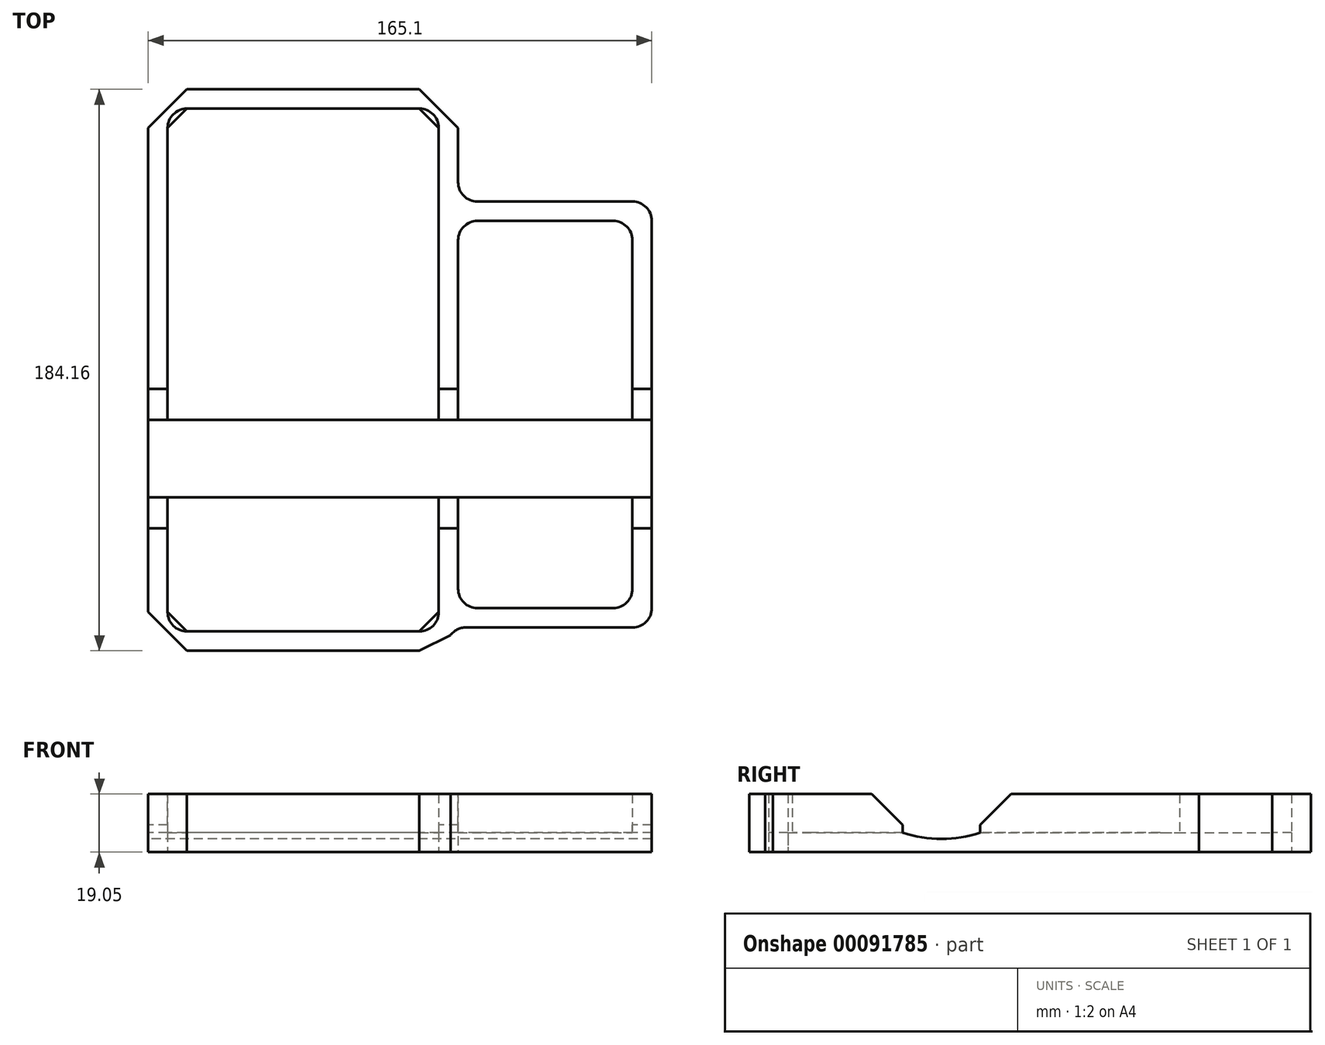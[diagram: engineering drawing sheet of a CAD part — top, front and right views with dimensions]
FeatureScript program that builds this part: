
annotation { "Feature Type Name" : "Feature", "Feature Type Description" : "" }
export const myFeature = defineFeature(function(context is Context, id is Id, definition is map)
    precondition{}
    {
        {
            var Q0;
            Q0=qCreatedBy(makeId("Top.planeOp"),FACE);
            var sketch = newSketch(context, id + "F0", { "sketchPlane" : qUnion([Q0])});
            skLineSegment(sketch, "E0.bottom", {"start": v(-38.1, 85.72) * mm, "end": v(38.1, 85.72) * mm});
            skLineSegment(sketch, "E0.top", {"start": v(-38.1, -85.73) * mm, "end": v(38.1, -85.73) * mm});
            skLineSegment(sketch, "E0.left", {"start": v(-44.45, 79.38) * mm, "end": v(-44.45, -79.38) * mm});
            skLineSegment(sketch, "E0.right", {"start": v(44.45, 79.38) * mm, "end": v(44.45, -79.38) * mm});
            skPoint(sketch, "E0.middle", {"position": v(0, 0) * mm});
            skPoint(sketch, "E1.visualSharp", {"position": v(-44.45, 85.72) * mm});
            skArc(sketch, "E1.filletArc", {"start": v(-38.1, 85.72) * mm, "mid": v(-42.6, 83.87) * mm, "end": v(-44.45, 79.38) * mm});
            skPoint(sketch, "E2.visualSharp", {"position": v(44.45, 85.72) * mm});
            skArc(sketch, "E2.filletArc", {"start": v(44.45, 79.38) * mm, "mid": v(42.6, 83.87) * mm, "end": v(38.1, 85.72) * mm});
            skPoint(sketch, "E3.visualSharp", {"position": v(44.45, -85.73) * mm});
            skArc(sketch, "E3.filletArc", {"start": v(38.1, -85.73) * mm, "mid": v(42.6, -83.87) * mm, "end": v(44.45, -79.38) * mm});
            skPoint(sketch, "E4.visualSharp", {"position": v(-44.45, -85.73) * mm});
            skArc(sketch, "E4.filletArc", {"start": v(-44.45, -79.38) * mm, "mid": v(-42.6, -83.87) * mm, "end": v(-38.1, -85.73) * mm});
            skArc(sketch, "E5.0", {"start": v(50.8, 79.38) * mm, "mid": v(47.08, 88.36) * mm, "end": v(38.1, 92.07) * mm});
            skLineSegment(sketch, "E5.1", {"start": v(-38.1, 92.08) * mm, "end": v(38.1, 92.08) * mm});
            skLineSegment(sketch, "E5.2", {"start": v(50.8, 79.38) * mm, "end": v(50.8, 61.61) * mm});
            skArc(sketch, "E5.3", {"start": v(-38.1, 92.07) * mm, "mid": v(-47.08, 88.36) * mm, "end": v(-50.8, 79.38) * mm});
            skArc(sketch, "E5.4", {"start": v(38.1, -92.08) * mm, "mid": v(43.79, -90.73) * mm, "end": v(48.27, -86.98) * mm});
            skLineSegment(sketch, "E5.5", {"start": v(-38.1, -92.08) * mm, "end": v(38.1, -92.08) * mm});
            skArc(sketch, "E5.6", {"start": v(-50.8, -79.38) * mm, "mid": v(-47.08, -88.36) * mm, "end": v(-38.1, -92.08) * mm});
            skLineSegment(sketch, "E5.7", {"start": v(-50.8, 79.38) * mm, "end": v(-50.8, -79.38) * mm});
            skLineSegment(sketch, "E6.bottom", {"start": v(57.15, -78.09) * mm, "end": v(101.6, -78.09) * mm});
            skLineSegment(sketch, "E6.top", {"start": v(57.15, 48.91) * mm, "end": v(101.6, 48.91) * mm});
            skLineSegment(sketch, "E6.left", {"start": v(50.8, -71.74) * mm, "end": v(50.8, 42.56) * mm});
            skLineSegment(sketch, "E6.right", {"start": v(107.95, -71.74) * mm, "end": v(107.95, 42.56) * mm});
            skPoint(sketch, "E6.middle", {"position": v(79.38, -14.59) * mm});
            skLineSegment(sketch, "E7.0", {"start": v(53.35, -84.44) * mm, "end": v(107.95, -84.44) * mm});
            skLineSegment(sketch, "E7.1", {"start": v(114.3, -78.09) * mm, "end": v(114.3, 48.91) * mm});
            skLineSegment(sketch, "E7.2", {"start": v(57.15, 55.26) * mm, "end": v(107.95, 55.26) * mm});
            skPoint(sketch, "E8.visualSharp", {"position": v(107.95, 48.91) * mm});
            skArc(sketch, "E8.filletArc", {"start": v(107.95, 42.56) * mm, "mid": v(106.1, 47.05) * mm, "end": v(101.6, 48.91) * mm});
            skPoint(sketch, "E9.visualSharp", {"position": v(107.95, -78.09) * mm});
            skArc(sketch, "E9.filletArc", {"start": v(101.6, -78.09) * mm, "mid": v(106.1, -76.23) * mm, "end": v(107.95, -71.74) * mm});
            skPoint(sketch, "E10.visualSharp", {"position": v(114.3, -84.44) * mm});
            skArc(sketch, "E10.filletArc", {"start": v(107.95, -84.44) * mm, "mid": v(112.44, -82.58) * mm, "end": v(114.3, -78.09) * mm});
            skPoint(sketch, "E11.visualSharp", {"position": v(114.3, 55.26) * mm});
            skArc(sketch, "E11.filletArc", {"start": v(114.3, 48.91) * mm, "mid": v(112.44, 53.4) * mm, "end": v(107.95, 55.26) * mm});
            skArc(sketch, "E12.filletArc", {"start": v(50.8, 61.61) * mm, "mid": v(52.66, 57.12) * mm, "end": v(57.15, 55.26) * mm});
            skPoint(sketch, "E13.visualSharp", {"position": v(50.8, 48.91) * mm});
            skArc(sketch, "E13.filletArc", {"start": v(57.15, 48.91) * mm, "mid": v(52.66, 47.05) * mm, "end": v(50.8, 42.56) * mm});
            skPoint(sketch, "E14.visualSharp", {"position": v(50.8, -78.09) * mm});
            skArc(sketch, "E14.filletArc", {"start": v(50.8, -71.74) * mm, "mid": v(52.66, -76.23) * mm, "end": v(57.15, -78.09) * mm});
            skArc(sketch, "E15.filletArc", {"start": v(53.35, -84.44) * mm, "mid": v(50.5, -85.11) * mm, "end": v(48.27, -86.98) * mm});
            skLineSegment(sketch, "E16", {"start": v(38.1, 85.72) * mm, "end": v(44.45, 79.38) * mm});
            skLineSegment(sketch, "E17", {"start": v(38.1, 92.07) * mm, "end": v(50.8, 79.38) * mm});
            skLineSegment(sketch, "E18", {"start": v(-44.45, 79.38) * mm, "end": v(-38.1, 85.72) * mm});
            skLineSegment(sketch, "E19", {"start": v(-38.15, 93.54) * mm, "end": v(-47.04, 96.44) * mm});
            skLineSegment(sketch, "E20", {"start": v(-38.1, 92.08) * mm, "end": v(-50.8, 79.38) * mm});
            skLineSegment(sketch, "E21", {"start": v(-44.45, -79.38) * mm, "end": v(-38.1, -85.73) * mm});
            skLineSegment(sketch, "E22", {"start": v(-50.8, -79.38) * mm, "end": v(-38.1, -92.08) * mm});
            skLineSegment(sketch, "E23", {"start": v(38.1, -85.73) * mm, "end": v(44.45, -79.38) * mm});
            skLineSegment(sketch, "E24", {"start": v(38.1, -92.08) * mm, "end": v(48.27, -86.98) * mm});
            skSolve(sketch);
        }
        {
            var Q0;
            Q0=makeQuery(id+"F0.imprint","IMPRINT",FACE,{"disambiguationData":[TD([[makeQuery(id+"F0.imprint","IMPRINT",EDGE,{"derivedFrom":sQuery(id+"F0.wireOp",EDGE,"E0.bottom")}),-1.0]])]});
            var Q1;
            Q1=makeQuery(id+"F0.imprint","IMPRINT",FACE,{"disambiguationData":[TD([[makeQuery(id+"F0.imprint","IMPRINT",EDGE,{"derivedFrom":sQuery(id+"F0.wireOp",EDGE,"E6.bottom")}),1.0]])]});
            var Q2;
            Q2=makeQuery(id+"F0.imprint","IMPRINT",FACE,{"disambiguationData":[TD([[makeQuery(id+"F0.imprint","IMPRINT",EDGE,{"derivedFrom":sQuery(id+"F0.wireOp",EDGE,"E0.bottom")}),1.0]])]});
            extrude(context, id + "F1", {"entities" : qUnion([Q0, Q1, Q2]), "depth" : 6.35 * mm});
        }
        {
            var Q0;
            Q0=makeQuery(id+"F0.imprint","IMPRINT",FACE,{"disambiguationData":[TD([[makeQuery(id+"F0.imprint","IMPRINT",EDGE,{"derivedFrom":sQuery(id+"F0.wireOp",EDGE,"E0.bottom")}),1.0]])]});
            extrude(context, id + "F2", {"entities" : qUnion([Q0]), "operationType" : NewBodyOperationType.ADD, "depth" : 19.05 * mm});
        }
        {
            var Q0;
            Q0=qCreatedBy(makeId("Right.planeOp"),FACE);
            var sketch = newSketch(context, id + "F3", { "sketchPlane" : qUnion([Q0])});
            skLineSegment(sketch, "E25", {"start": v(-16.4, 6.35) * mm, "end": v(-16.4, 53.7) * mm});
            skLineSegment(sketch, "E26", {"start": v(-16.4, 53.7) * mm, "end": v(-41.8, 53.7) * mm});
            skLineSegment(sketch, "E27", {"start": v(-41.8, 53.7) * mm, "end": v(-41.8, 6.35) * mm});
            skArc(sketch, "E28", {"start": v(-41.8, 6.35) * mm, "mid": v(-29.1, 4.35) * mm, "end": v(-16.4, 6.35) * mm});
            skSolve(sketch);
        }
        {
            var Q0;
            Q0=makeQuery(id+"F3.imprint","IMPRINT",FACE,{"disambiguationData":[TD([[makeQuery(id+"F3.imprint","IMPRINT",EDGE,{"derivedFrom":sQuery(id+"F3.wireOp",EDGE,"E25")}),1.0]])]});
            extrude(context, id + "F4", {"entities" : qUnion([Q0]), "operationType" : NewBodyOperationType.REMOVE, "endBound" : BoundingType.SYMMETRIC, "depth" : 254 * mm});
        }
        {
            var Q0;
            Q0=makeQuery(id+"F4.boolean.opBoolean","INTERSECT",EDGE,{"disambiguationData":[OD(1.0)],"derivedFrom":[makeQuery(id+"F2.opExtrude","CAP_FACE",FACE,{"disambiguationData":[OSD([sQuery(id+"F0.wireOp",EDGE,"E0.bottom"),sQuery(id+"F0.wireOp",EDGE,"E0.top"),sQuery(id+"F0.wireOp",EDGE,"E0.left"),sQuery(id+"F0.wireOp",EDGE,"E0.right"),sQuery(id+"F0.wireOp",EDGE,"E1.filletArc"),sQuery(id+"F0.wireOp",EDGE,"E2.filletArc"),sQuery(id+"F0.wireOp",EDGE,"E3.filletArc"),sQuery(id+"F0.wireOp",EDGE,"E4.filletArc"),sQuery(id+"F0.wireOp",EDGE,"E5.0"),sQuery(id+"F0.wireOp",EDGE,"E5.1"),sQuery(id+"F0.wireOp",EDGE,"E5.2"),sQuery(id+"F0.wireOp",EDGE,"E5.3"),sQuery(id+"F0.wireOp",EDGE,"E5.4"),sQuery(id+"F0.wireOp",EDGE,"E5.5"),sQuery(id+"F0.wireOp",EDGE,"E5.6"),sQuery(id+"F0.wireOp",EDGE,"E5.7"),sQuery(id+"F0.wireOp",EDGE,"E6.bottom"),sQuery(id+"F0.wireOp",EDGE,"E6.top"),sQuery(id+"F0.wireOp",EDGE,"E6.left"),sQuery(id+"F0.wireOp",EDGE,"E6.right"),sQuery(id+"F0.wireOp",EDGE,"E7.0"),sQuery(id+"F0.wireOp",EDGE,"E7.1"),sQuery(id+"F0.wireOp",EDGE,"E7.2"),sQuery(id+"F0.wireOp",EDGE,"E8.filletArc"),sQuery(id+"F0.wireOp",EDGE,"E9.filletArc"),sQuery(id+"F0.wireOp",EDGE,"E10.filletArc"),sQuery(id+"F0.wireOp",EDGE,"E11.filletArc"),sQuery(id+"F0.wireOp",EDGE,"E12.filletArc"),sQuery(id+"F0.wireOp",EDGE,"E13.filletArc"),sQuery(id+"F0.wireOp",EDGE,"E14.filletArc"),sQuery(id+"F0.wireOp",EDGE,"E15.filletArc")])],"isStart":false}),makeQuery(id+"F4.opExtrude","SWEPT_FACE",FACE,{"disambiguationData":[OSD([sQuery(id+"F3.wireOp",EDGE,"E25")])]})]});
            var Q1;
            Q1=makeQuery(id+"F4.boolean.opBoolean","INTERSECT",EDGE,{"disambiguationData":[OD(1.0)],"derivedFrom":[makeQuery(id+"F2.opExtrude","CAP_FACE",FACE,{"disambiguationData":[OSD([sQuery(id+"F0.wireOp",EDGE,"E0.bottom"),sQuery(id+"F0.wireOp",EDGE,"E0.top"),sQuery(id+"F0.wireOp",EDGE,"E0.left"),sQuery(id+"F0.wireOp",EDGE,"E0.right"),sQuery(id+"F0.wireOp",EDGE,"E1.filletArc"),sQuery(id+"F0.wireOp",EDGE,"E2.filletArc"),sQuery(id+"F0.wireOp",EDGE,"E3.filletArc"),sQuery(id+"F0.wireOp",EDGE,"E4.filletArc"),sQuery(id+"F0.wireOp",EDGE,"E5.0"),sQuery(id+"F0.wireOp",EDGE,"E5.1"),sQuery(id+"F0.wireOp",EDGE,"E5.2"),sQuery(id+"F0.wireOp",EDGE,"E5.3"),sQuery(id+"F0.wireOp",EDGE,"E5.4"),sQuery(id+"F0.wireOp",EDGE,"E5.5"),sQuery(id+"F0.wireOp",EDGE,"E5.6"),sQuery(id+"F0.wireOp",EDGE,"E5.7"),sQuery(id+"F0.wireOp",EDGE,"E6.bottom"),sQuery(id+"F0.wireOp",EDGE,"E6.top"),sQuery(id+"F0.wireOp",EDGE,"E6.left"),sQuery(id+"F0.wireOp",EDGE,"E6.right"),sQuery(id+"F0.wireOp",EDGE,"E7.0"),sQuery(id+"F0.wireOp",EDGE,"E7.1"),sQuery(id+"F0.wireOp",EDGE,"E7.2"),sQuery(id+"F0.wireOp",EDGE,"E8.filletArc"),sQuery(id+"F0.wireOp",EDGE,"E9.filletArc"),sQuery(id+"F0.wireOp",EDGE,"E10.filletArc"),sQuery(id+"F0.wireOp",EDGE,"E11.filletArc"),sQuery(id+"F0.wireOp",EDGE,"E12.filletArc"),sQuery(id+"F0.wireOp",EDGE,"E13.filletArc"),sQuery(id+"F0.wireOp",EDGE,"E14.filletArc"),sQuery(id+"F0.wireOp",EDGE,"E15.filletArc")])],"isStart":false}),makeQuery(id+"F4.opExtrude","SWEPT_FACE",FACE,{"disambiguationData":[OSD([sQuery(id+"F3.wireOp",EDGE,"E27")])]})]});
            var Q2;
            Q2=makeQuery(id+"F4.boolean.opBoolean","INTERSECT",EDGE,{"disambiguationData":[OD(2.0)],"derivedFrom":[makeQuery(id+"F2.opExtrude","CAP_FACE",FACE,{"disambiguationData":[OSD([sQuery(id+"F0.wireOp",EDGE,"E0.bottom"),sQuery(id+"F0.wireOp",EDGE,"E0.top"),sQuery(id+"F0.wireOp",EDGE,"E0.left"),sQuery(id+"F0.wireOp",EDGE,"E0.right"),sQuery(id+"F0.wireOp",EDGE,"E1.filletArc"),sQuery(id+"F0.wireOp",EDGE,"E2.filletArc"),sQuery(id+"F0.wireOp",EDGE,"E3.filletArc"),sQuery(id+"F0.wireOp",EDGE,"E4.filletArc"),sQuery(id+"F0.wireOp",EDGE,"E5.0"),sQuery(id+"F0.wireOp",EDGE,"E5.1"),sQuery(id+"F0.wireOp",EDGE,"E5.2"),sQuery(id+"F0.wireOp",EDGE,"E5.3"),sQuery(id+"F0.wireOp",EDGE,"E5.4"),sQuery(id+"F0.wireOp",EDGE,"E5.5"),sQuery(id+"F0.wireOp",EDGE,"E5.6"),sQuery(id+"F0.wireOp",EDGE,"E5.7"),sQuery(id+"F0.wireOp",EDGE,"E6.bottom"),sQuery(id+"F0.wireOp",EDGE,"E6.top"),sQuery(id+"F0.wireOp",EDGE,"E6.left"),sQuery(id+"F0.wireOp",EDGE,"E6.right"),sQuery(id+"F0.wireOp",EDGE,"E7.0"),sQuery(id+"F0.wireOp",EDGE,"E7.1"),sQuery(id+"F0.wireOp",EDGE,"E7.2"),sQuery(id+"F0.wireOp",EDGE,"E8.filletArc"),sQuery(id+"F0.wireOp",EDGE,"E9.filletArc"),sQuery(id+"F0.wireOp",EDGE,"E10.filletArc"),sQuery(id+"F0.wireOp",EDGE,"E11.filletArc"),sQuery(id+"F0.wireOp",EDGE,"E12.filletArc"),sQuery(id+"F0.wireOp",EDGE,"E13.filletArc"),sQuery(id+"F0.wireOp",EDGE,"E14.filletArc"),sQuery(id+"F0.wireOp",EDGE,"E15.filletArc")])],"isStart":false}),makeQuery(id+"F4.opExtrude","SWEPT_FACE",FACE,{"disambiguationData":[OSD([sQuery(id+"F3.wireOp",EDGE,"E25")])]})]});
            var Q3;
            Q3=makeQuery(id+"F4.boolean.opBoolean","INTERSECT",EDGE,{"disambiguationData":[OD(2.0)],"derivedFrom":[makeQuery(id+"F2.opExtrude","CAP_FACE",FACE,{"disambiguationData":[OSD([sQuery(id+"F0.wireOp",EDGE,"E0.bottom"),sQuery(id+"F0.wireOp",EDGE,"E0.top"),sQuery(id+"F0.wireOp",EDGE,"E0.left"),sQuery(id+"F0.wireOp",EDGE,"E0.right"),sQuery(id+"F0.wireOp",EDGE,"E1.filletArc"),sQuery(id+"F0.wireOp",EDGE,"E2.filletArc"),sQuery(id+"F0.wireOp",EDGE,"E3.filletArc"),sQuery(id+"F0.wireOp",EDGE,"E4.filletArc"),sQuery(id+"F0.wireOp",EDGE,"E5.0"),sQuery(id+"F0.wireOp",EDGE,"E5.1"),sQuery(id+"F0.wireOp",EDGE,"E5.2"),sQuery(id+"F0.wireOp",EDGE,"E5.3"),sQuery(id+"F0.wireOp",EDGE,"E5.4"),sQuery(id+"F0.wireOp",EDGE,"E5.5"),sQuery(id+"F0.wireOp",EDGE,"E5.6"),sQuery(id+"F0.wireOp",EDGE,"E5.7"),sQuery(id+"F0.wireOp",EDGE,"E6.bottom"),sQuery(id+"F0.wireOp",EDGE,"E6.top"),sQuery(id+"F0.wireOp",EDGE,"E6.left"),sQuery(id+"F0.wireOp",EDGE,"E6.right"),sQuery(id+"F0.wireOp",EDGE,"E7.0"),sQuery(id+"F0.wireOp",EDGE,"E7.1"),sQuery(id+"F0.wireOp",EDGE,"E7.2"),sQuery(id+"F0.wireOp",EDGE,"E8.filletArc"),sQuery(id+"F0.wireOp",EDGE,"E9.filletArc"),sQuery(id+"F0.wireOp",EDGE,"E10.filletArc"),sQuery(id+"F0.wireOp",EDGE,"E11.filletArc"),sQuery(id+"F0.wireOp",EDGE,"E12.filletArc"),sQuery(id+"F0.wireOp",EDGE,"E13.filletArc"),sQuery(id+"F0.wireOp",EDGE,"E14.filletArc"),sQuery(id+"F0.wireOp",EDGE,"E15.filletArc")])],"isStart":false}),makeQuery(id+"F4.opExtrude","SWEPT_FACE",FACE,{"disambiguationData":[OSD([sQuery(id+"F3.wireOp",EDGE,"E27")])]})]});
            var Q4;
            Q4=makeQuery(id+"F4.boolean.opBoolean","INTERSECT",EDGE,{"disambiguationData":[OD(0.0)],"derivedFrom":[makeQuery(id+"F2.opExtrude","CAP_FACE",FACE,{"disambiguationData":[OSD([sQuery(id+"F0.wireOp",EDGE,"E0.bottom"),sQuery(id+"F0.wireOp",EDGE,"E0.top"),sQuery(id+"F0.wireOp",EDGE,"E0.left"),sQuery(id+"F0.wireOp",EDGE,"E0.right"),sQuery(id+"F0.wireOp",EDGE,"E1.filletArc"),sQuery(id+"F0.wireOp",EDGE,"E2.filletArc"),sQuery(id+"F0.wireOp",EDGE,"E3.filletArc"),sQuery(id+"F0.wireOp",EDGE,"E4.filletArc"),sQuery(id+"F0.wireOp",EDGE,"E5.0"),sQuery(id+"F0.wireOp",EDGE,"E5.1"),sQuery(id+"F0.wireOp",EDGE,"E5.2"),sQuery(id+"F0.wireOp",EDGE,"E5.3"),sQuery(id+"F0.wireOp",EDGE,"E5.4"),sQuery(id+"F0.wireOp",EDGE,"E5.5"),sQuery(id+"F0.wireOp",EDGE,"E5.6"),sQuery(id+"F0.wireOp",EDGE,"E5.7"),sQuery(id+"F0.wireOp",EDGE,"E6.bottom"),sQuery(id+"F0.wireOp",EDGE,"E6.top"),sQuery(id+"F0.wireOp",EDGE,"E6.left"),sQuery(id+"F0.wireOp",EDGE,"E6.right"),sQuery(id+"F0.wireOp",EDGE,"E7.0"),sQuery(id+"F0.wireOp",EDGE,"E7.1"),sQuery(id+"F0.wireOp",EDGE,"E7.2"),sQuery(id+"F0.wireOp",EDGE,"E8.filletArc"),sQuery(id+"F0.wireOp",EDGE,"E9.filletArc"),sQuery(id+"F0.wireOp",EDGE,"E10.filletArc"),sQuery(id+"F0.wireOp",EDGE,"E11.filletArc"),sQuery(id+"F0.wireOp",EDGE,"E12.filletArc"),sQuery(id+"F0.wireOp",EDGE,"E13.filletArc"),sQuery(id+"F0.wireOp",EDGE,"E14.filletArc"),sQuery(id+"F0.wireOp",EDGE,"E15.filletArc")])],"isStart":false}),makeQuery(id+"F4.opExtrude","SWEPT_FACE",FACE,{"disambiguationData":[OSD([sQuery(id+"F3.wireOp",EDGE,"E25")])]})]});
            var Q5;
            Q5=makeQuery(id+"F4.boolean.opBoolean","INTERSECT",EDGE,{"disambiguationData":[OD(0.0)],"derivedFrom":[makeQuery(id+"F2.opExtrude","CAP_FACE",FACE,{"disambiguationData":[OSD([sQuery(id+"F0.wireOp",EDGE,"E0.bottom"),sQuery(id+"F0.wireOp",EDGE,"E0.top"),sQuery(id+"F0.wireOp",EDGE,"E0.left"),sQuery(id+"F0.wireOp",EDGE,"E0.right"),sQuery(id+"F0.wireOp",EDGE,"E1.filletArc"),sQuery(id+"F0.wireOp",EDGE,"E2.filletArc"),sQuery(id+"F0.wireOp",EDGE,"E3.filletArc"),sQuery(id+"F0.wireOp",EDGE,"E4.filletArc"),sQuery(id+"F0.wireOp",EDGE,"E5.0"),sQuery(id+"F0.wireOp",EDGE,"E5.1"),sQuery(id+"F0.wireOp",EDGE,"E5.2"),sQuery(id+"F0.wireOp",EDGE,"E5.3"),sQuery(id+"F0.wireOp",EDGE,"E5.4"),sQuery(id+"F0.wireOp",EDGE,"E5.5"),sQuery(id+"F0.wireOp",EDGE,"E5.6"),sQuery(id+"F0.wireOp",EDGE,"E5.7"),sQuery(id+"F0.wireOp",EDGE,"E6.bottom"),sQuery(id+"F0.wireOp",EDGE,"E6.top"),sQuery(id+"F0.wireOp",EDGE,"E6.left"),sQuery(id+"F0.wireOp",EDGE,"E6.right"),sQuery(id+"F0.wireOp",EDGE,"E7.0"),sQuery(id+"F0.wireOp",EDGE,"E7.1"),sQuery(id+"F0.wireOp",EDGE,"E7.2"),sQuery(id+"F0.wireOp",EDGE,"E8.filletArc"),sQuery(id+"F0.wireOp",EDGE,"E9.filletArc"),sQuery(id+"F0.wireOp",EDGE,"E10.filletArc"),sQuery(id+"F0.wireOp",EDGE,"E11.filletArc"),sQuery(id+"F0.wireOp",EDGE,"E12.filletArc"),sQuery(id+"F0.wireOp",EDGE,"E13.filletArc"),sQuery(id+"F0.wireOp",EDGE,"E14.filletArc"),sQuery(id+"F0.wireOp",EDGE,"E15.filletArc")])],"isStart":false}),makeQuery(id+"F4.opExtrude","SWEPT_FACE",FACE,{"disambiguationData":[OSD([sQuery(id+"F3.wireOp",EDGE,"E27")])]})]});
            chamfer(context, id + "F5", {"entities" : qUnion([Q0, Q1, Q2, Q3, Q4, Q5]), "width" : 10.16 * mm, "tangentPropagation" : true});
        }
    });
